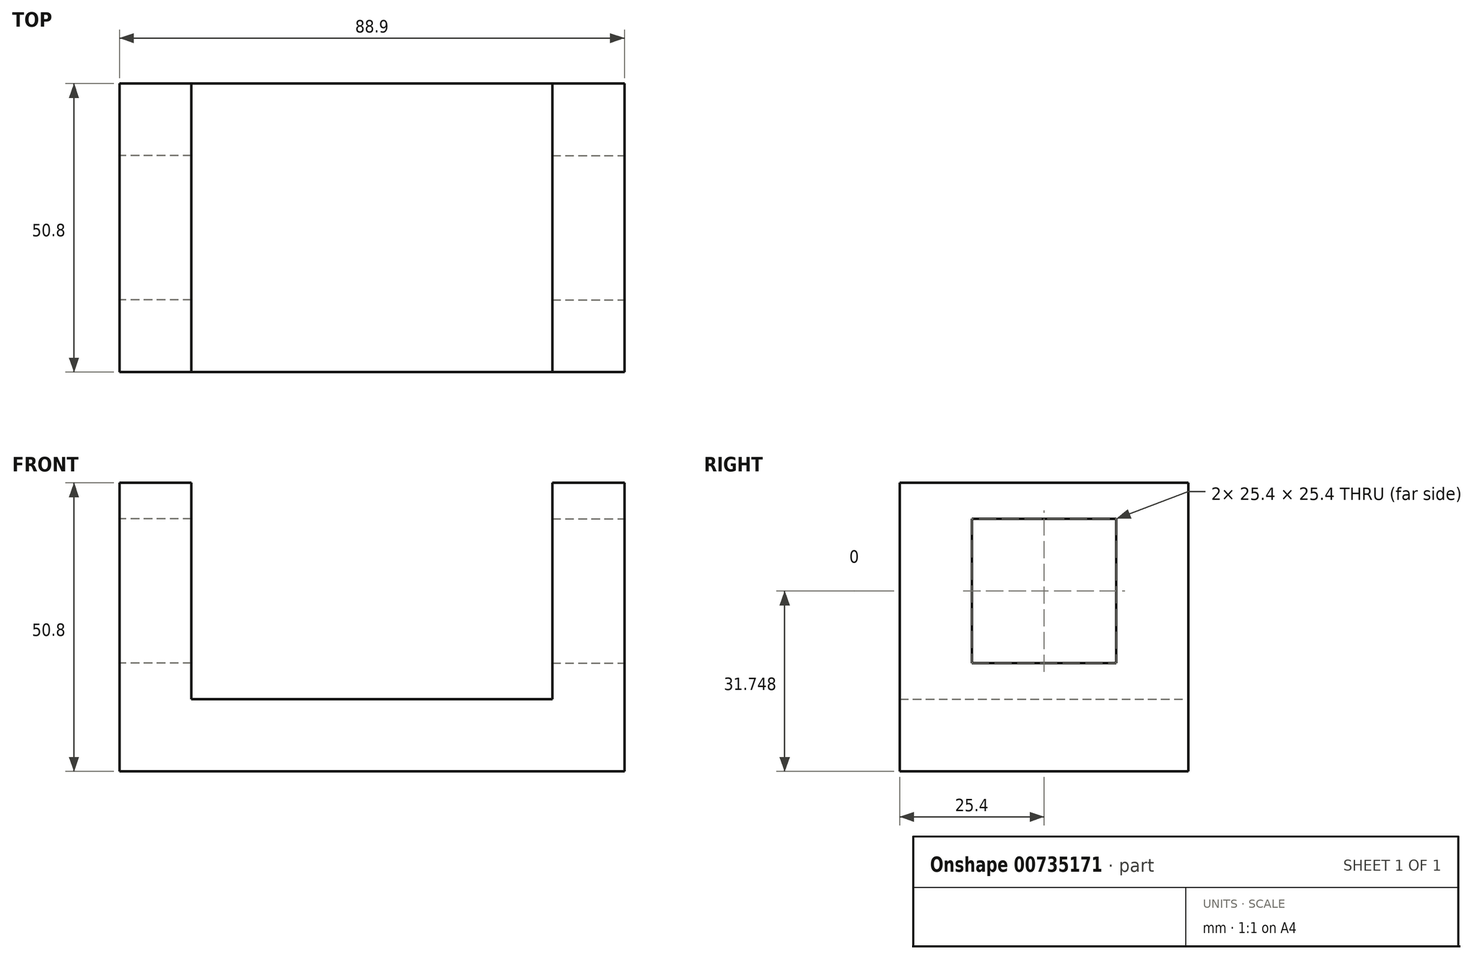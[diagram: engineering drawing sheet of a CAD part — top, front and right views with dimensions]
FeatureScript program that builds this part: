
annotation { "Feature Type Name" : "Feature", "Feature Type Description" : "" }
export const myFeature = defineFeature(function(context is Context, id is Id, definition is map)
    precondition{}
    {
        {
            var Q0;
            Q0=qCreatedBy(makeId("Front.planeOp"),FACE);
            var sketch = newSketch(context, id + "F0", { "sketchPlane" : qUnion([Q0])});
            skLineSegment(sketch, "E0", {"start": v(-70.82, 27.66) * mm, "end": v(-70.82, -23.14) * mm});
            skLineSegment(sketch, "E1", {"start": v(-70.82, -23.14) * mm, "end": v(18.08, -23.14) * mm});
            skLineSegment(sketch, "E2", {"start": v(18.08, -23.14) * mm, "end": v(18.08, 27.66) * mm});
            skLineSegment(sketch, "E3", {"start": v(18.08, 27.66) * mm, "end": v(5.38, 27.66) * mm});
            skLineSegment(sketch, "E4", {"start": v(-70.82, 27.66) * mm, "end": v(-58.12, 27.66) * mm});
            skLineSegment(sketch, "E5", {"start": v(-58.12, 27.66) * mm, "end": v(-58.12, -10.44) * mm});
            skLineSegment(sketch, "E6", {"start": v(5.38, 27.66) * mm, "end": v(5.38, -10.44) * mm});
            skLineSegment(sketch, "E7", {"start": v(5.38, -10.44) * mm, "end": v(-58.12, -10.44) * mm});
            skSolve(sketch);
        }
        {
            var Q0;
            Q0=makeQuery(id+"F0.imprint","IMPRINT",FACE,{"disambiguationData":[TD([[makeQuery(id+"F0.imprint","IMPRINT",EDGE,{"derivedFrom":sQuery(id+"F0.wireOp",EDGE,"E0")}),1.0]])]});
            extrude(context, id + "F1", {"entities" : qUnion([Q0]), "depth" : 50.8 * mm, "offsetDistance" : 25.4 * mm});
        }
        {
            var Q0;
            Q0=makeQuery(id+"F1.opExtrude","SWEPT_FACE",FACE,{"disambiguationData":[OSD([sQuery(id+"F0.wireOp",EDGE,"E2")])]});
            var sketch = newSketch(context, id + "F2", { "sketchPlane" : qUnion([Q0])});
            skLineSegment(sketch, "E8", {"start": v(-38.1, 21.3) * mm, "end": v(-12.7, 21.3) * mm});
            skLineSegment(sketch, "E9", {"start": v(-38.1, 21.3) * mm, "end": v(-38.1, -4.1) * mm});
            skLineSegment(sketch, "E10", {"start": v(-12.7, 21.3) * mm, "end": v(-12.7, -4.1) * mm});
            skLineSegment(sketch, "E11", {"start": v(-12.7, -4.1) * mm, "end": v(-38.1, -4.1) * mm});
            skSolve(sketch);
        }
        {
            var Q0;
            Q0 = qSketchRegion(id + "F2", true);
            extrude(context, id + "F3", {"entities" : qUnion([Q0]), "operationType" : NewBodyOperationType.REMOVE, "oppositeDirection" : true, "depth" : 12.7 * mm, "offsetDistance" : 25.4 * mm});
        }
        {
            var Q0;
            Q0=makeQuery(id+"F1.opExtrude","SWEPT_FACE",FACE,{"disambiguationData":[OSD([sQuery(id+"F0.wireOp",EDGE,"E0")])]});
            var sketch = newSketch(context, id + "F4", { "sketchPlane" : qUnion([Q0])});
            skLineSegment(sketch, "E12", {"start": v(12.7, 21.3) * mm, "end": v(38.1, 21.3) * mm});
            skLineSegment(sketch, "E13", {"start": v(38.1, 21.3) * mm, "end": v(38.1, -4.1) * mm});
            skLineSegment(sketch, "E14", {"start": v(12.7, 21.3) * mm, "end": v(12.7, -4.1) * mm});
            skLineSegment(sketch, "E15", {"start": v(12.7, -4.1) * mm, "end": v(38.1, -4.1) * mm});
            skSolve(sketch);
        }
        {
            var Q0;
            Q0=makeQuery(id+"F4.imprint","IMPRINT",FACE,{"disambiguationData":[TD([[makeQuery(id+"F4.imprint","IMPRINT",EDGE,{"derivedFrom":sQuery(id+"F4.wireOp",EDGE,"E12")}),-1.0]])]});
            extrude(context, id + "F5", {"entities" : qUnion([Q0]), "operationType" : NewBodyOperationType.REMOVE, "oppositeDirection" : true, "depth" : 12.7 * mm, "offsetDistance" : 25.4 * mm});
        }
    });
